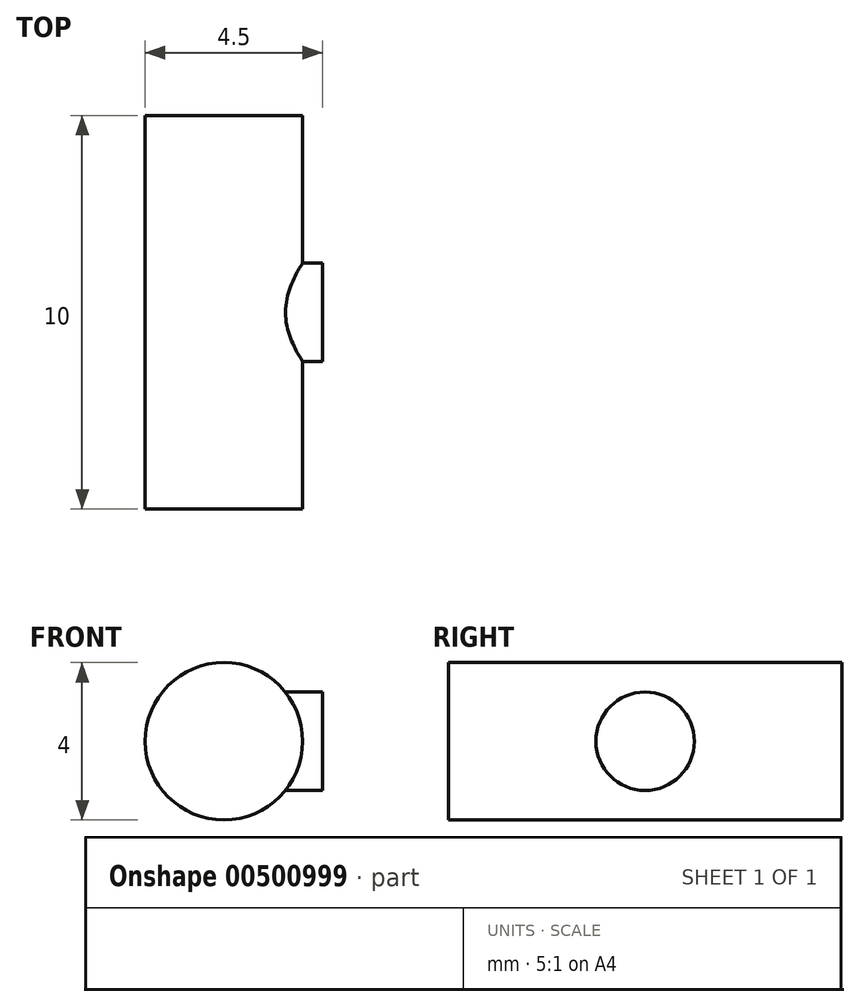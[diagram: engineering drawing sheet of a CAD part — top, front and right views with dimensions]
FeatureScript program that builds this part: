
annotation { "Feature Type Name" : "Feature", "Feature Type Description" : "" }
export const myFeature = defineFeature(function(context is Context, id is Id, definition is map)
    precondition{}
    {
        {
            var Q0;
            Q0=qCreatedBy(makeId("Right.planeOp"),FACE);
            var sketch = newSketch(context, id + "F0", { "sketchPlane" : qUnion([Q0])});
            skLineSegment(sketch, "E0.top", {"start": v(-5, -2) * mm, "end": v(5, -2) * mm});
            skLineSegment(sketch, "E0.right", {"start": v(5, 0) * mm, "end": v(5, -2) * mm});
            skPoint(sketch, "E1.orphan", {"position": v(0, 1.55) * mm});
            skPoint(sketch, "E2.start.orphan", {"position": v(0, 0) * mm});
            skLineSegment(sketch, "E3", {"start": v(0, 0) * mm, "end": v(10, 0) * mm, "construction": true});
            skLineSegment(sketch, "E4", {"start": v(-5, -2) * mm, "end": v(-5, 0) * mm});
            skLineSegment(sketch, "E5", {"start": v(-5, 0) * mm, "end": v(5, 0) * mm});
            skSolve(sketch);
        }
        {
            var Q0;
            Q0 = qSketchRegion(id + "F0", true);
            var Q1;
            Q1=sQuery(id+"F0.wireOp",EDGE,"E3");
            revolve(context, id + "F1", {"entities" : qUnion([Q0]), "axis" : qUnion([Q1]), "revolveType" : RevolveType.FULL});
        }
        {
            var Q0;
            Q0=qCreatedBy(makeId("Right.planeOp"),FACE);
            var sketch = newSketch(context, id + "F2", { "sketchPlane" : qUnion([Q0])});
            skCircle(sketch, "E6", {"center": v(0, 0) * mm, "radius": 1.25 * mm});
            skSolve(sketch);
        }
        {
            var Q0;
            Q0 = qSketchRegion(id + "F2", true);
            extrude(context, id + "F3", {"entities" : qUnion([Q0]), "operationType" : NewBodyOperationType.ADD, "depth" : 2.5 * mm});
        }
    });
